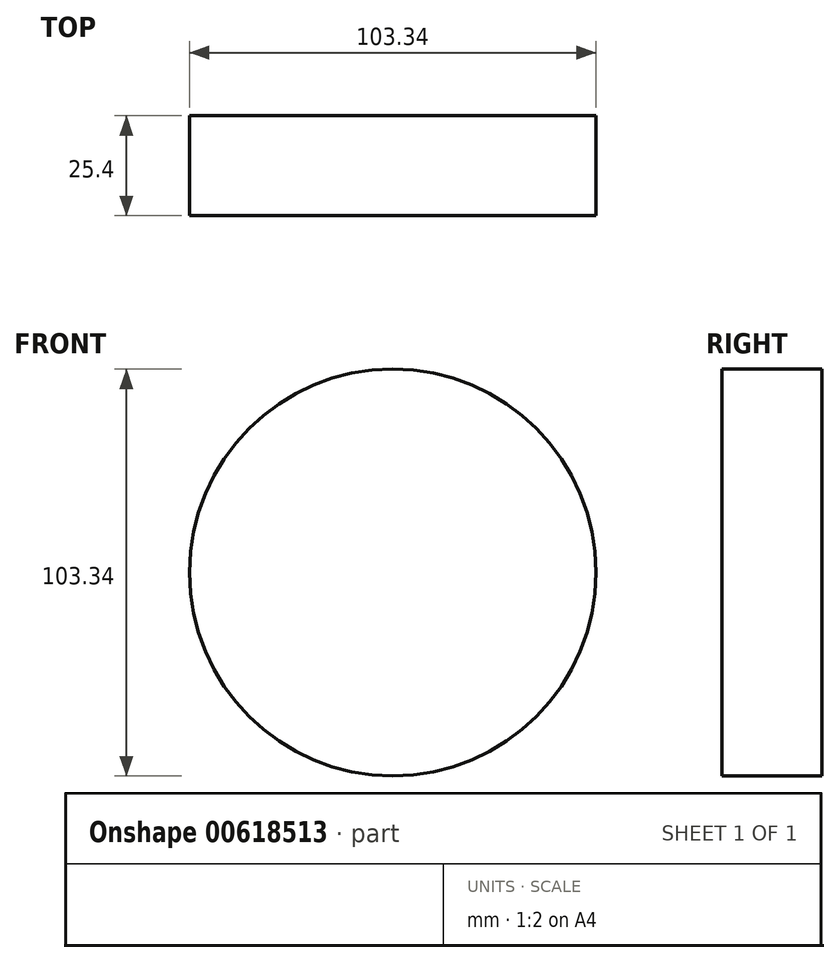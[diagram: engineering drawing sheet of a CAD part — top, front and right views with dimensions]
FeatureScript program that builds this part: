
annotation { "Feature Type Name" : "Feature", "Feature Type Description" : "" }
export const myFeature = defineFeature(function(context is Context, id is Id, definition is map)
    precondition{}
    {
        {
            var Q0;
            Q0=qCreatedBy(makeId("Front.planeOp"),FACE);
            var sketch = newSketch(context, id + "F0", { "sketchPlane" : qUnion([Q0])});
            skCircle(sketch, "E0", {"center": v(-48.56, 57.76) * mm, "radius": 51.67 * mm});
            skSolve(sketch);
        }
        {
            var Q0;
            Q0 = qSketchRegion(id + "F0", true);
            extrude(context, id + "F1", {"entities" : qUnion([Q0]), "depth" : 25.4 * mm, "offsetDistance" : 25.4 * mm});
        }
    });
